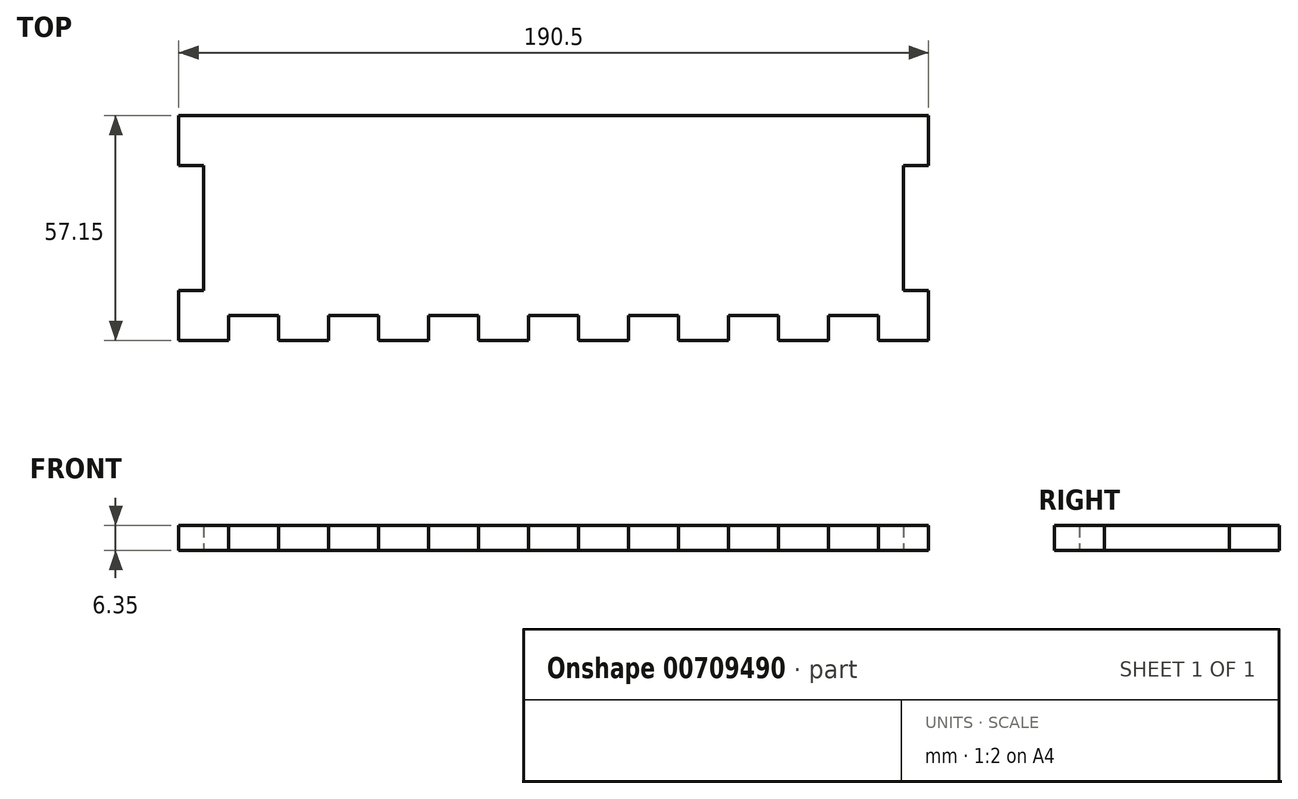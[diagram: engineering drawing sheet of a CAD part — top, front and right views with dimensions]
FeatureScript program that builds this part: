
annotation { "Feature Type Name" : "Feature", "Feature Type Description" : "" }
export const myFeature = defineFeature(function(context is Context, id is Id, definition is map)
    precondition{}
    {
        {
            var Q0;
            Q0=qCreatedBy(makeId("Top.planeOp"),FACE);
            var sketch = newSketch(context, id + "F0", { "sketchPlane" : qUnion([Q0])});
            skLineSegment(sketch, "E0.bottom", {"start": v(0, 0) * mm, "end": v(190.5, 0) * mm});
            skLineSegment(sketch, "E0.top", {"start": v(0, -57.15) * mm, "end": v(12.7, -57.15) * mm});
            skLineSegment(sketch, "E0.left", {"start": v(0, 0) * mm, "end": v(0, -12.7) * mm});
            skLineSegment(sketch, "E1", {"start": v(12.7, -57.15) * mm, "end": v(12.7, -50.8) * mm});
            skLineSegment(sketch, "E2", {"start": v(12.7, -50.8) * mm, "end": v(25.4, -50.8) * mm});
            skLineSegment(sketch, "E3", {"start": v(25.4, -50.8) * mm, "end": v(25.4, -57.15) * mm});
            skLineSegment(sketch, "E4", {"start": v(25.4, -57.15) * mm, "end": v(38.1, -57.15) * mm});
            skLineSegment(sketch, "E5", {"start": v(38.1, -57.15) * mm, "end": v(38.1, -50.8) * mm});
            skLineSegment(sketch, "E6", {"start": v(38.1, -50.8) * mm, "end": v(50.8, -50.8) * mm});
            skLineSegment(sketch, "E7", {"start": v(50.8, -50.8) * mm, "end": v(50.8, -57.15) * mm});
            skLineSegment(sketch, "E8", {"start": v(50.8, -57.15) * mm, "end": v(63.5, -57.15) * mm});
            skLineSegment(sketch, "E9", {"start": v(63.5, -57.15) * mm, "end": v(63.5, -50.8) * mm});
            skLineSegment(sketch, "E10", {"start": v(63.5, -50.8) * mm, "end": v(76.2, -50.8) * mm});
            skLineSegment(sketch, "E11", {"start": v(76.2, -50.8) * mm, "end": v(76.2, -57.15) * mm});
            skLineSegment(sketch, "E12", {"start": v(76.2, -57.15) * mm, "end": v(88.9, -57.15) * mm});
            skLineSegment(sketch, "E13", {"start": v(88.9, -57.15) * mm, "end": v(88.9, -50.8) * mm});
            skLineSegment(sketch, "E14", {"start": v(88.9, -50.8) * mm, "end": v(101.6, -50.8) * mm});
            skLineSegment(sketch, "E15", {"start": v(101.6, -50.8) * mm, "end": v(101.6, -57.15) * mm});
            skLineSegment(sketch, "E16.trimOffspring", {"start": v(101.6, -57.15) * mm, "end": v(114.3, -57.15) * mm});
            skLineSegment(sketch, "E17", {"start": v(114.3, -57.15) * mm, "end": v(114.3, -50.8) * mm});
            skLineSegment(sketch, "E18", {"start": v(114.3, -50.8) * mm, "end": v(127, -50.8) * mm});
            skLineSegment(sketch, "E19", {"start": v(127, -50.8) * mm, "end": v(127, -57.15) * mm});
            skLineSegment(sketch, "E20", {"start": v(127, -57.15) * mm, "end": v(139.7, -57.15) * mm});
            skLineSegment(sketch, "E21", {"start": v(139.7, -57.15) * mm, "end": v(139.7, -50.8) * mm});
            skLineSegment(sketch, "E22", {"start": v(139.7, -50.8) * mm, "end": v(152.4, -50.8) * mm});
            skLineSegment(sketch, "E23", {"start": v(152.4, -50.8) * mm, "end": v(152.4, -57.15) * mm});
            skLineSegment(sketch, "E24", {"start": v(152.4, -57.15) * mm, "end": v(165.1, -57.15) * mm});
            skLineSegment(sketch, "E25", {"start": v(165.1, -57.15) * mm, "end": v(165.1, -50.8) * mm});
            skLineSegment(sketch, "E26", {"start": v(165.1, -50.8) * mm, "end": v(177.8, -50.8) * mm});
            skLineSegment(sketch, "E27", {"start": v(177.8, -50.8) * mm, "end": v(177.8, -57.15) * mm});
            skLineSegment(sketch, "E28.trimOffspring", {"start": v(177.8, -57.15) * mm, "end": v(190.5, -57.15) * mm});
            skLineSegment(sketch, "E29", {"start": v(0, -57.15) * mm, "end": v(0, -44.45) * mm});
            skLineSegment(sketch, "E30", {"start": v(0, -44.45) * mm, "end": v(6.35, -44.45) * mm});
            skLineSegment(sketch, "E31", {"start": v(6.35, -44.45) * mm, "end": v(6.35, -12.7) * mm});
            skLineSegment(sketch, "E32", {"start": v(6.35, -12.7) * mm, "end": v(0, -12.7) * mm});
            skLineSegment(sketch, "E33.trimOffspring", {"start": v(0, -44.45) * mm, "end": v(0, -57.15) * mm});
            skLineSegment(sketch, "E34", {"start": v(95.25, -50.8) * mm, "end": v(95.25, -31.75) * mm, "construction": true});
            skLineSegment(sketch, "E35.MirrorCS", {"start": v(190.5, 0) * mm, "end": v(190.5, -12.7) * mm});
            skLineSegment(sketch, "E36.MirrorCS", {"start": v(184.15, -12.7) * mm, "end": v(190.5, -12.7) * mm});
            skLineSegment(sketch, "E37.MirrorCS", {"start": v(184.15, -44.45) * mm, "end": v(184.15, -12.7) * mm});
            skLineSegment(sketch, "E38.MirrorCS", {"start": v(190.5, -44.45) * mm, "end": v(184.15, -44.45) * mm});
            skLineSegment(sketch, "E39.MirrorCS", {"start": v(190.5, -57.15) * mm, "end": v(190.5, -44.45) * mm});
            skSolve(sketch);
        }
        {
            var Q0;
            Q0=makeQuery(id+"F0.imprint","IMPRINT",FACE,{"disambiguationData":[TD([[makeQuery(id+"F0.imprint","IMPRINT",EDGE,{"derivedFrom":sQuery(id+"F0.wireOp",EDGE,"E0.bottom")}),-1.0]])]});
            extrude(context, id + "F1", {"entities" : qUnion([Q0]), "depth" : 6.35 * mm, "offsetDistance" : 25.4 * mm});
        }
    });
